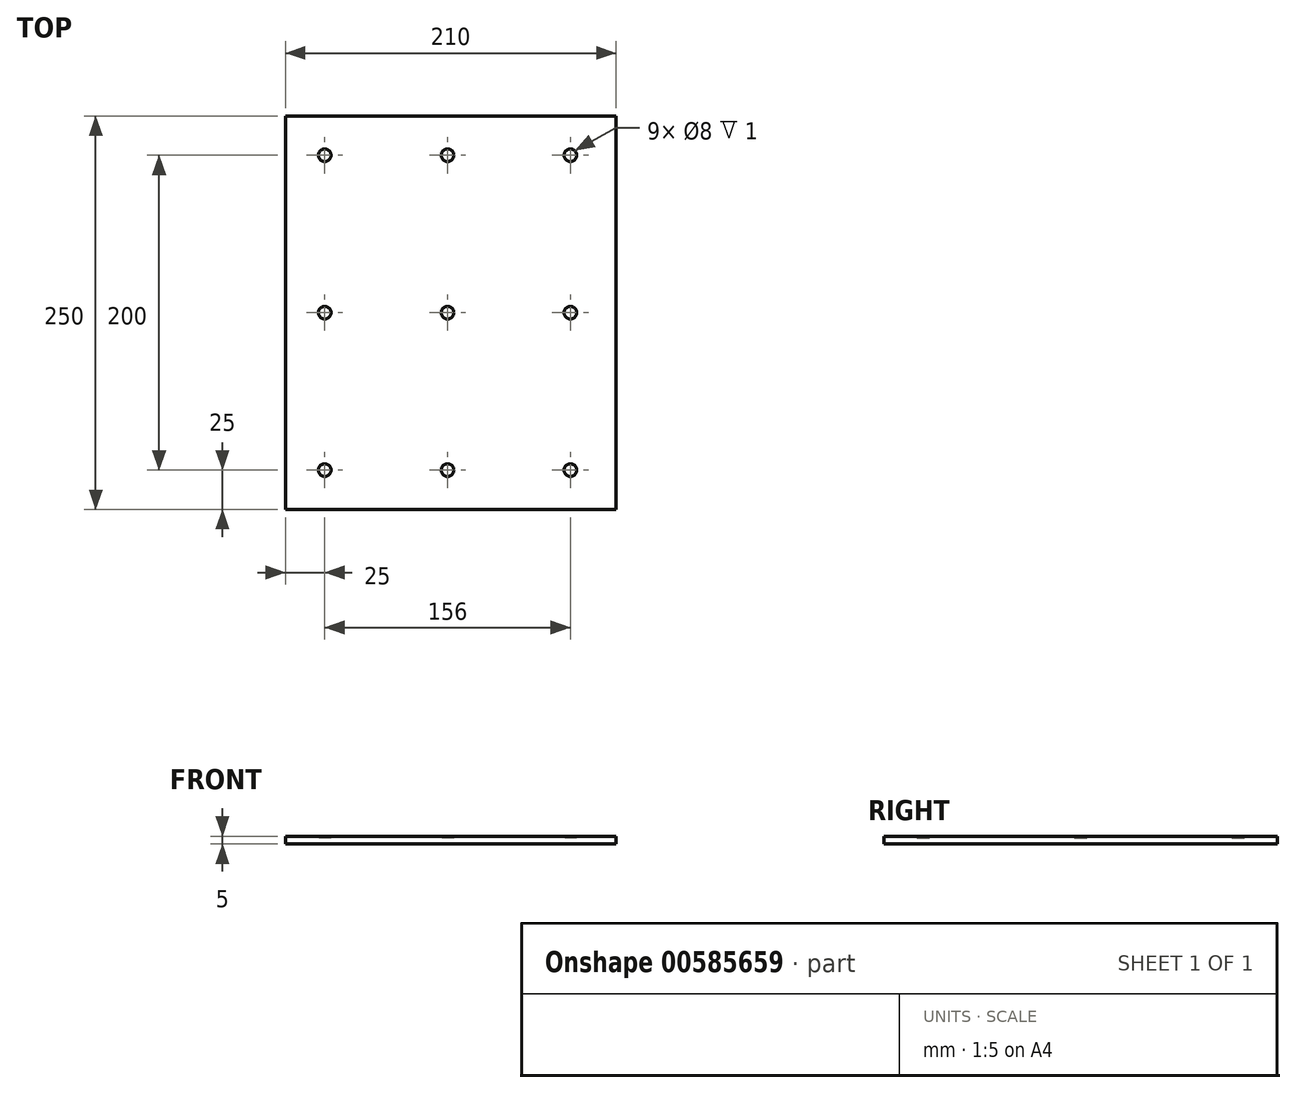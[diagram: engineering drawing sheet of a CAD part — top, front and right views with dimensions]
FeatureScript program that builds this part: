
annotation { "Feature Type Name" : "Feature", "Feature Type Description" : "" }
export const myFeature = defineFeature(function(context is Context, id is Id, definition is map)
    precondition{}
    {
        {
            var Q0;
            Q0=qCreatedBy(makeId("Top.planeOp"),FACE);
            var sketch = newSketch(context, id + "F0", { "sketchPlane" : qUnion([Q0])});
            skLineSegment(sketch, "E0.bottom", {"start": v(-105, 125) * mm, "end": v(105, 125) * mm});
            skLineSegment(sketch, "E0.top", {"start": v(-105, -125) * mm, "end": v(105, -125) * mm});
            skLineSegment(sketch, "E0.left", {"start": v(-105, 125) * mm, "end": v(-105, -125) * mm});
            skLineSegment(sketch, "E0.right", {"start": v(105, 125) * mm, "end": v(105, -125) * mm});
            skSolve(sketch);
        }
        {
            var Q0;
            Q0 = qSketchRegion(id + "F0", true);
            extrude(context, id + "F1", {"entities" : qUnion([Q0]), "depth" : 5 * mm, "offsetDistance" : 25 * mm});
        }
        {
            var Q0;
            Q0=makeQuery(id+"F1.opExtrude","CAP_FACE",FACE,{"disambiguationData":[OSD([sQuery(id+"F0.wireOp",EDGE,"E0.bottom"),sQuery(id+"F0.wireOp",EDGE,"E0.top"),sQuery(id+"F0.wireOp",EDGE,"E0.left"),sQuery(id+"F0.wireOp",EDGE,"E0.right")])],"isStart":false});
            var sketch = newSketch(context, id + "F2", { "sketchPlane" : qUnion([Q0])});
            skCircle(sketch, "E1", {"center": v(-80, -100) * mm, "radius": 4 * mm});
            skCircle(sketch, "E2.0.1.0", {"center": v(-80, 0) * mm, "radius": 4 * mm});
            skCircle(sketch, "E2.0.2.0", {"center": v(-80, 100) * mm, "radius": 4 * mm});
            skCircle(sketch, "E2.1.0.0", {"center": v(-2, -100) * mm, "radius": 4 * mm});
            skCircle(sketch, "E2.1.1.0", {"center": v(-2, 0) * mm, "radius": 4 * mm});
            skCircle(sketch, "E2.1.2.0", {"center": v(-2, 100) * mm, "radius": 4 * mm});
            skCircle(sketch, "E2.2.0.0", {"center": v(76, -100) * mm, "radius": 4 * mm});
            skCircle(sketch, "E2.2.1.0", {"center": v(76, 0) * mm, "radius": 4 * mm});
            skCircle(sketch, "E2.2.2.0", {"center": v(76, 100) * mm, "radius": 4 * mm});
            skLineSegment(sketch, "E2.direction1", {"start": v(-80, -100) * mm, "end": v(-2, -100) * mm, "construction": true});
            skLineSegment(sketch, "E2.direction2", {"start": v(-80, -100) * mm, "end": v(-80, 0) * mm, "construction": true});
            skSolve(sketch);
        }
        {
            var Q0;
            Q0 = qSketchRegion(id + "F2", true);
            extrude(context, id + "F3", {"entities" : qUnion([Q0]), "operationType" : NewBodyOperationType.REMOVE, "oppositeDirection" : true, "depth" : 1 * mm, "offsetDistance" : 25 * mm});
        }
    });
